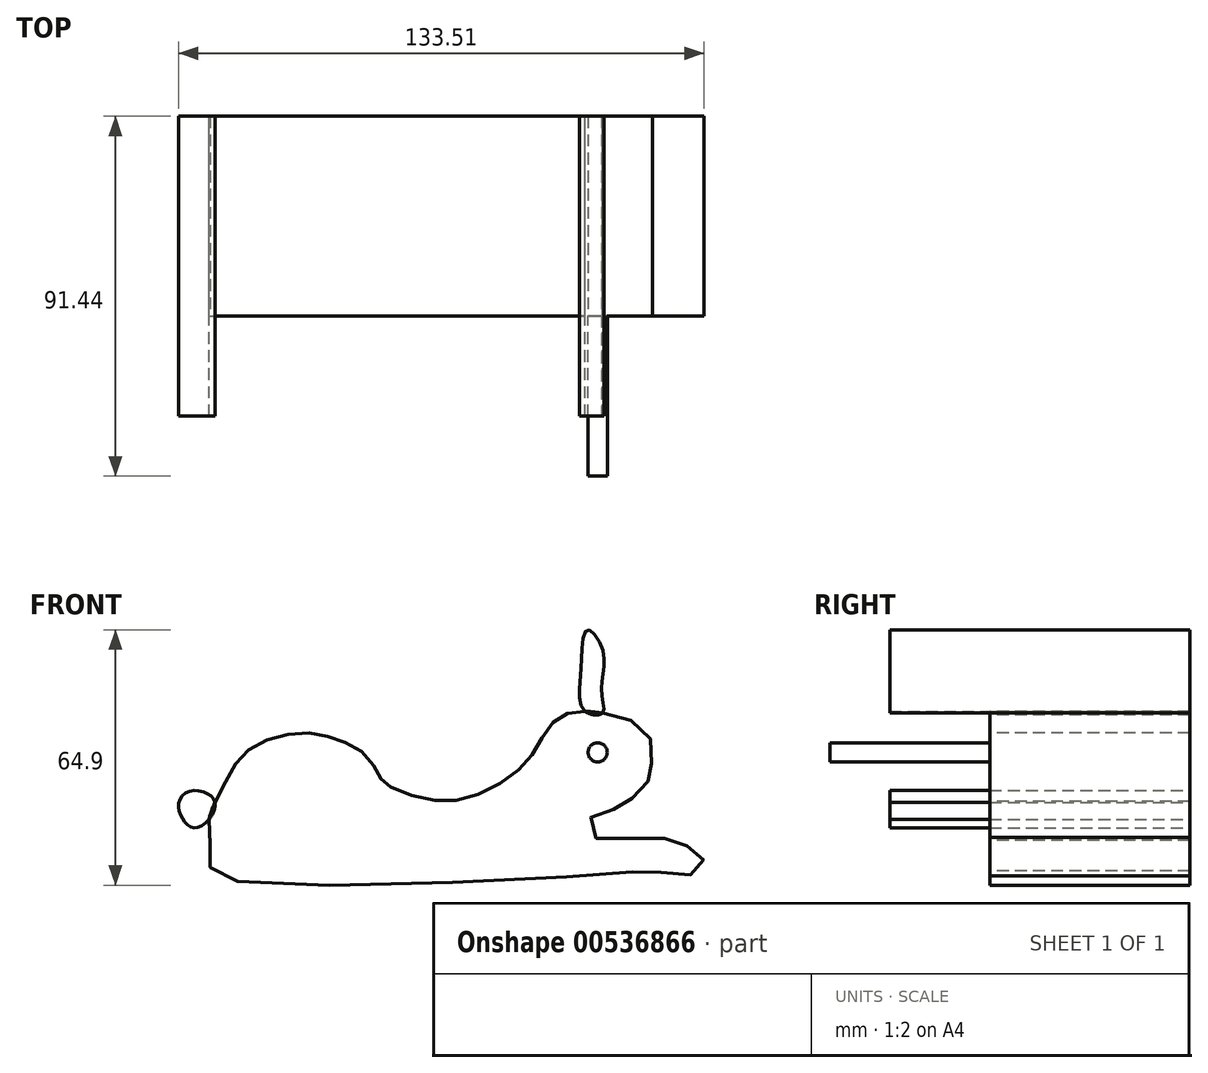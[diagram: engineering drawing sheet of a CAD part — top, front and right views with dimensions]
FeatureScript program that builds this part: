
annotation { "Feature Type Name" : "Feature", "Feature Type Description" : "" }
export const myFeature = defineFeature(function(context is Context, id is Id, definition is map)
    precondition{}
    {
        {
            var Q0;
            Q0=qCreatedBy(makeId("Front.planeOp"),FACE);
            var sketch = newSketch(context, id + "F0", { "sketchPlane" : qUnion([Q0])});
            skFitSpline(sketch, "E0", {"points": [v(56.9, 13.86) * mm, v(56.9, 19.7) * mm, v(52.53, 24.8) * mm, v(44.5, 27) * mm, v(36.72, 27.24) * mm, v(31.37, 24.08) * mm, v(27.24, 17.27) * mm, v(20.91, 10.7) * mm, v(9.73, 5.35) * mm, v(0, 5.1) * mm, v(-10.21, 8.75) * mm, v(-12.16, 10.94) * mm, v(-15.56, 16.3) * mm, v(-21.89, 19.94) * mm, v(-29.18, 21.89) * mm, v(-38.67, 20.91) * mm, v(-46.7, 16.54) * mm, v(-51.31, 9.48) * mm, v(-55.45, 0) * mm, v(-55.2, -6.08) * mm, v(-55.2, -11.43) * mm, v(-52.53, -14.83) * mm, v(45.72, -13.86) * mm, v(58.6, -13.38) * mm, v(66.88, -14.1) * mm, v(70.28, -10.94) * mm, v(67.85, -8.03) * mm, v(63.47, -5.6) * mm, v(57.88, -4.62) * mm, v(53.26, -4.86) * mm, v(48.88, -4.86) * mm, v(43.04, -4.86) * mm, v(41.1, 0) * mm, v(45.96, 1.95) * mm, v(49.85, 4.13) * mm, v(53.99, 6.8) * mm, v(56.66, 11.19) * mm, v(56.9, 13.86) * mm]});
            skFitSpline(sketch, "E1", {"points": [v(40.12, 27.46) * mm, v(38.67, 33.8) * mm, v(39.15, 39.88) * mm, v(40.61, 48.15) * mm, v(44.5, 43.29) * mm, v(44.5, 36.48) * mm, v(44.5, 30.4) * mm, v(44.5, 27) * mm, v(40.12, 27.46) * mm]});
            skFitSpline(sketch, "E2", {"points": [v(-53.95, 4.36) * mm, v(-56.42, 6.8) * mm, v(-61.28, 6.8) * mm, v(-63.23, 3.4) * mm, v(-62.01, 0) * mm, v(-59.34, -2.19) * mm, v(-55.45, 0) * mm, v(-53.95, 4.36) * mm]});
            skSolve(sketch);
        }
        {
            var Q0;
            {var subQ0=sQuery(id+"F0.wireOp",EDGE,"E2");var subQ1=sQuery(id+"F0.wireOp",EDGE,"E0");var subQ2=makeQuery(id+"F0.imprint","INTERSECT",VERTEX,{"disambiguationData":[OD(0.0)],"derivedFrom":[subQ1,subQ0]});Q0=makeQuery(id+"F0.imprint","IMPRINT",FACE,{"disambiguationData":[TD([[makeQuery(id+"F0.imprint","IMPRINT",EDGE,{"disambiguationData":[TD([[subQ2,-1.0]])],"derivedFrom":subQ1}),-1.0]])]});}
            var Q1;
            {var subQ0=sQuery(id+"F0.wireOp",EDGE,"E1");var subQ1=sQuery(id+"F0.wireOp",EDGE,"E0");var subQ2=makeQuery(id+"F0.imprint","INTERSECT",VERTEX,{"disambiguationData":[OD(0.0)],"derivedFrom":[subQ1,subQ0]});Q1=makeQuery(id+"F0.imprint","IMPRINT",FACE,{"disambiguationData":[TD([[makeQuery(id+"F0.imprint","IMPRINT",EDGE,{"disambiguationData":[TD([[subQ2,1.0]])],"derivedFrom":subQ1}),-1.0]])]});}
            var Q2;
            {var subQ0=sQuery(id+"F0.wireOp",EDGE,"E1");var subQ1=sQuery(id+"F0.wireOp",EDGE,"E0");var subQ2=makeQuery(id+"F0.imprint","INTERSECT",VERTEX,{"disambiguationData":[OD(0.0)],"derivedFrom":[subQ1,subQ0]});Q2=makeQuery(id+"F0.imprint","IMPRINT",FACE,{"disambiguationData":[TD([[makeQuery(id+"F0.imprint","IMPRINT",EDGE,{"disambiguationData":[TD([[subQ2,-1.0]])],"derivedFrom":subQ1}),1.0]])]});}
            extrude(context, id + "F1", {"entities" : qUnion([Q0, Q1, Q2]), "depth" : 76.2 * mm, "offsetDistance" : 25.4 * mm});
        }
        {
            var Q0;
            Q0=makeQuery(id+"F1.opExtrude","CAP_FACE",FACE,{"disambiguationData":[OSD([sQuery(id+"F0.wireOp",EDGE,"E0"),sQuery(id+"F0.wireOp",EDGE,"E1"),sQuery(id+"F0.wireOp",EDGE,"E2")])],"isStart":false});
            var sketch = newSketch(context, id + "F2", { "sketchPlane" : qUnion([Q0])});
            skCircle(sketch, "E3", {"center": v(43.29, 17.02) * mm, "radius": 2.43 * mm});
            skSolve(sketch);
        }
        {
            var Q0;
            Q0=makeQuery(id+"F2.imprint","IMPRINT",FACE,{"disambiguationData":[TD([[makeQuery(id+"F2.imprint","IMPRINT",EDGE,{"derivedFrom":sQuery(id+"F2.wireOp",EDGE,"E3")}),1.0]])]});
            extrude(context, id + "F3", {"entities" : qUnion([Q0]), "operationType" : NewBodyOperationType.ADD, "depth" : 12.7 * mm, "offsetDistance" : 25.4 * mm});
        }
        {
            var Q0;
            Q0=makeQuery(id+"F3.opExtrude","CAP_FACE",FACE,{"disambiguationData":[OSD([sQuery(id+"F2.wireOp",EDGE,"E3")])],"isStart":false});
            extrude(context, id + "F4", {"entities" : qUnion([Q0]), "operationType" : NewBodyOperationType.ADD, "depth" : 2.54 * mm, "offsetDistance" : 25.4 * mm});
        }
        {
            var Q0;
            Q0=makeQuery(id+"F1.opExtrude","CAP_FACE",FACE,{"disambiguationData":[OSD([sQuery(id+"F0.wireOp",EDGE,"E0"),sQuery(id+"F0.wireOp",EDGE,"E1"),sQuery(id+"F0.wireOp",EDGE,"E2")])],"isStart":false});
            extrude(context, id + "F5", {"entities" : qUnion([Q0]), "operationType" : NewBodyOperationType.REMOVE, "oppositeDirection" : true, "depth" : 25.4 * mm, "offsetDistance" : 25.4 * mm});
        }
    });
